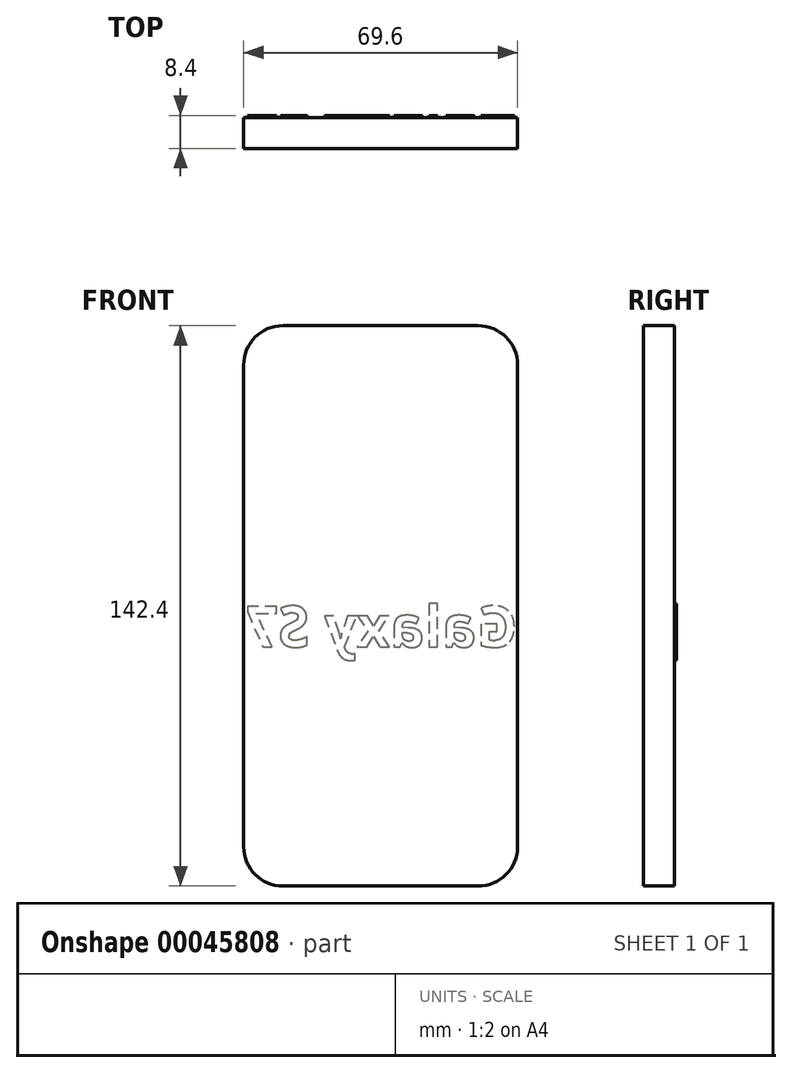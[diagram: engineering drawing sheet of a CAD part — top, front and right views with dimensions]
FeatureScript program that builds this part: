
annotation { "Feature Type Name" : "Feature", "Feature Type Description" : "" }
export const myFeature = defineFeature(function(context is Context, id is Id, definition is map)
    precondition{}
    {
        {
            var Q0;
            Q0=qCreatedBy(makeId("Front.planeOp"),FACE);
            var sketch = newSketch(context, id + "F0", { "sketchPlane" : qUnion([Q0])});
            skLineSegment(sketch, "E0.bottom", {"start": v(34.8, 71.2) * mm, "end": v(-34.8, 71.2) * mm});
            skLineSegment(sketch, "E0.top", {"start": v(34.8, -71.2) * mm, "end": v(-34.8, -71.2) * mm});
            skLineSegment(sketch, "E0.left", {"start": v(34.8, 71.2) * mm, "end": v(34.8, -71.2) * mm});
            skLineSegment(sketch, "E0.right", {"start": v(-34.8, 71.2) * mm, "end": v(-34.8, -71.2) * mm});
            skPoint(sketch, "E0.middle", {"position": v(0, 0) * mm});
            skSolve(sketch);
        }
        {
            var Q0;
            Q0 = qSketchRegion(id + "F0", true);
            extrude(context, id + "F1", {"entities" : qUnion([Q0]), "depth" : 7.9 * mm, "offsetDistance" : 25 * mm});
        }
        {
            var Q0;
            Q0=makeQuery(id+"F1.opExtrude","SWEPT_EDGE",EDGE,{"disambiguationData":[OSD([sQuery(id+"F0.wireOp",EDGE,"E0.bottom"),sQuery(id+"F0.wireOp",EDGE,"E0.right")])]});
            var Q1;
            Q1=makeQuery(id+"F1.opExtrude","SWEPT_EDGE",EDGE,{"disambiguationData":[OSD([sQuery(id+"F0.wireOp",EDGE,"E0.bottom"),sQuery(id+"F0.wireOp",EDGE,"E0.left")])]});
            var Q2;
            Q2=makeQuery(id+"F1.opExtrude","SWEPT_EDGE",EDGE,{"disambiguationData":[OSD([sQuery(id+"F0.wireOp",EDGE,"E0.top"),sQuery(id+"F0.wireOp",EDGE,"E0.right")])]});
            var Q3;
            Q3=makeQuery(id+"F1.opExtrude","SWEPT_EDGE",EDGE,{"disambiguationData":[OSD([sQuery(id+"F0.wireOp",EDGE,"E0.top"),sQuery(id+"F0.wireOp",EDGE,"E0.left")])]});
            fillet(context, id + "F2", {"entities" : qUnion([Q0, Q1, Q2, Q3]), "tangentPropagation" : true, "radius" : 10 * mm, "defaultsChanged" : true, "vertexSettings" : [], "allowEdgeOverflow" : false});
        }
        {
            var Q0;
            Q0=makeQuery(id+"F1.opExtrude","CAP_FACE",FACE,{"disambiguationData":[OSD([sQuery(id+"F0.wireOp",EDGE,"E0.bottom"),sQuery(id+"F0.wireOp",EDGE,"E0.top"),sQuery(id+"F0.wireOp",EDGE,"E0.left"),sQuery(id+"F0.wireOp",EDGE,"E0.right")])],"isStart":true});
            var sketch = newSketch(context, id + "F3", { "sketchPlane" : qUnion([Q0])});
            skText(sketch, "E1", { "text": "Galaxy S7", "fontName": "OpenSans-Bold.ttf"});
            const initialGuessF3  = {"E1": [-0.0348, -0.01044, 1, 0, 0.01044]};
            skSetInitialGuess(sketch, initialGuessF3);
            skSolve(sketch);
        }
        {
            var Q0;
            Q0 = qSketchRegion(id + "F3", true);
            extrude(context, id + "F4", {"entities" : qUnion([Q0]), "operationType" : NewBodyOperationType.ADD, "depth" : 0.5 * mm, "offsetDistance" : 25 * mm});
        }
    });
